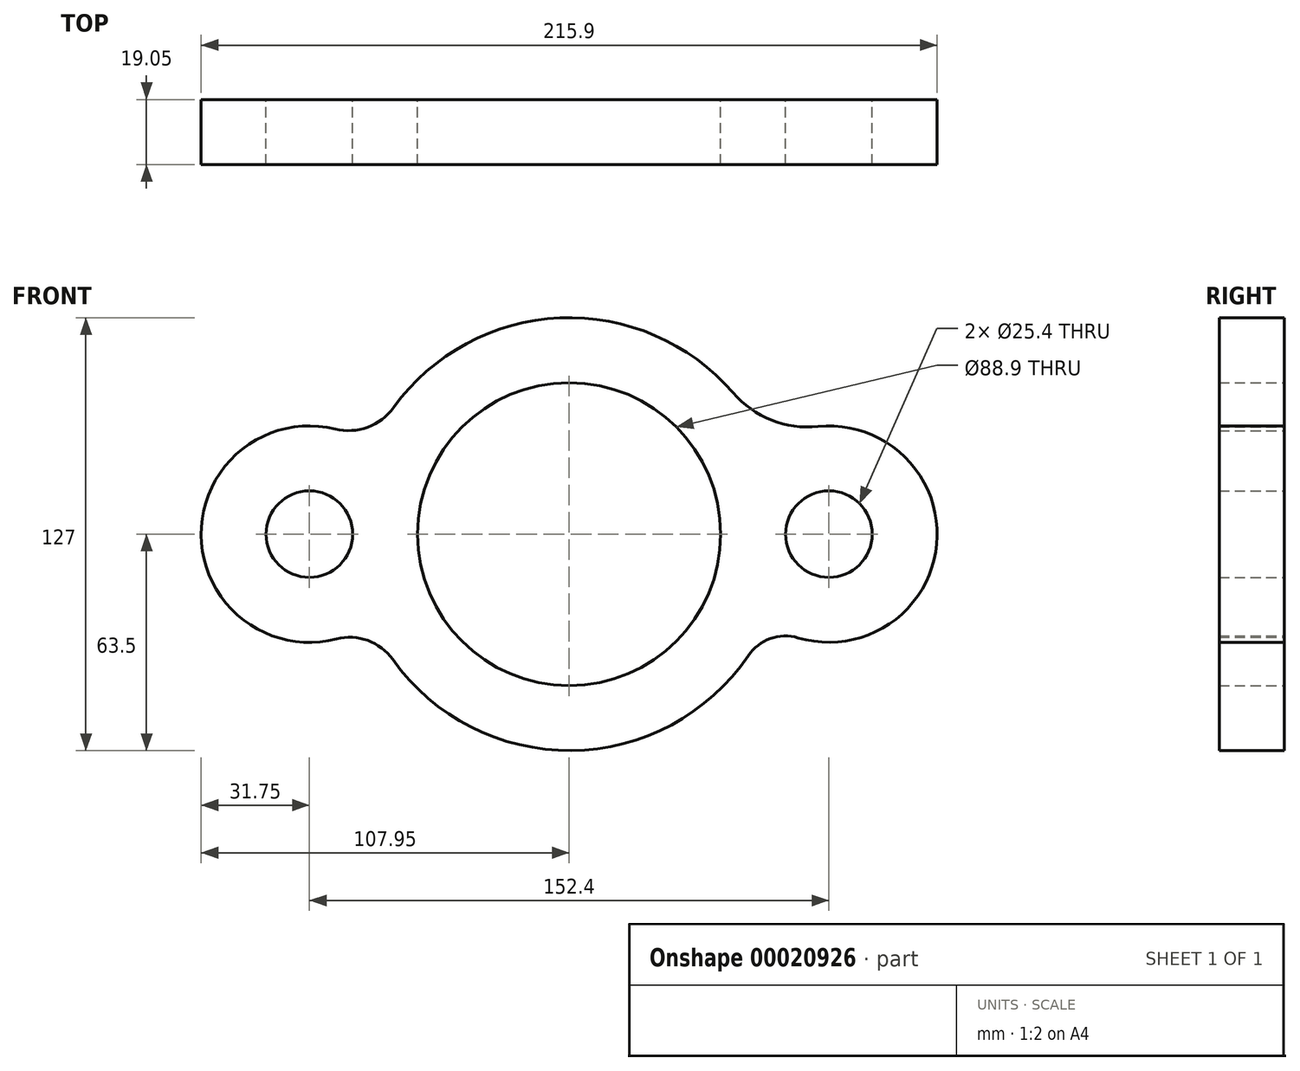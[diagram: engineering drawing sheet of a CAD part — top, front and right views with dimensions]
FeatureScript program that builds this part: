
annotation { "Feature Type Name" : "Feature", "Feature Type Description" : "" }
export const myFeature = defineFeature(function(context is Context, id is Id, definition is map)
    precondition{}
    {
        {
            var Q0;
            Q0=qCreatedBy(makeId("Front.planeOp"),FACE);
            var sketch = newSketch(context, id + "F0", { "sketchPlane" : qUnion([Q0])});
            skCircle(sketch, "E0", {"center": v(0, 0) * mm, "radius": 44.45 * mm});
            skCircle(sketch, "E1", {"center": v(-76.2, 0) * mm, "radius": 12.7 * mm});
            skCircle(sketch, "E2", {"center": v(76.2, 0) * mm, "radius": 12.7 * mm});
            skCircle(sketch, "E3", {"center": v(0, 0) * mm, "radius": 63.5 * mm});
            skCircle(sketch, "E4", {"center": v(76.2, 0) * mm, "radius": 31.75 * mm});
            skCircle(sketch, "E5", {"center": v(-76.2, 0) * mm, "radius": 31.75 * mm});
            skArc(sketch, "E6", {"start": v(48.07, 41.5) * mm, "mid": v(59.31, 33.5) * mm, "end": v(72.98, 31.59) * mm});
            skArc(sketch, "E7", {"start": v(-68.67, 30.84) * mm, "mid": v(-59.1, 31.39) * mm, "end": v(-51.48, 37.18) * mm});
            skArc(sketch, "E8", {"start": v(-51.78, -36.75) * mm, "mid": v(-59.08, -31.18) * mm, "end": v(-68.25, -30.74) * mm});
            skArc(sketch, "E9", {"start": v(67.18, -30.44) * mm, "mid": v(59, -30.67) * mm, "end": v(52.53, -35.67) * mm});
            skSolve(sketch);
        }
        {
            var Q0;
            {var subQ3=sQuery(id+"F0.wireOp",EDGE,"E0");var subQ5=sQuery(id+"F0.wireOp",EDGE,"E4");var subQ7=makeQuery(id+"F0.imprint","INTERSECT",VERTEX,{"derivedFrom":[subQ3,subQ5]});Q0=makeQuery(id+"F0.imprint","IMPRINT",FACE,{"disambiguationData":[TD([[makeQuery(id+"F0.imprint","IMPRINT",EDGE,{"disambiguationData":[TD([[subQ7,-1.0]])],"derivedFrom":subQ3}),-1.0]])]});}
            var Q1;
            {var subQ1=sQuery(id+"F0.wireOp",EDGE,"E3");var subQ5=makeQuery(id+"F0.imprint","INTERSECT",VERTEX,{"derivedFrom":[sQuery(id+"F0.wireOp",EDGE,"E1"),subQ1]});Q1=makeQuery(id+"F0.imprint","IMPRINT",FACE,{"disambiguationData":[TD([[makeQuery(id+"F0.imprint","IMPRINT",EDGE,{"disambiguationData":[TD([[subQ5,1.0]])],"derivedFrom":subQ1}),1.0]])]});}
            var Q2;
            {var subQ3=sQuery(id+"F0.wireOp",EDGE,"E0");var subQ5=sQuery(id+"F0.wireOp",EDGE,"E4");var subQ7=makeQuery(id+"F0.imprint","INTERSECT",VERTEX,{"derivedFrom":[subQ3,subQ5]});Q2=makeQuery(id+"F0.imprint","IMPRINT",FACE,{"disambiguationData":[TD([[makeQuery(id+"F0.imprint","IMPRINT",EDGE,{"disambiguationData":[TD([[subQ7,1.0]])],"derivedFrom":subQ3}),-1.0]])]});}
            var Q3;
            {var subQ1=sQuery(id+"F0.wireOp",EDGE,"E3");var subQ5=makeQuery(id+"F0.imprint","INTERSECT",VERTEX,{"derivedFrom":[sQuery(id+"F0.wireOp",EDGE,"E2"),subQ1]});Q3=makeQuery(id+"F0.imprint","IMPRINT",FACE,{"disambiguationData":[TD([[makeQuery(id+"F0.imprint","IMPRINT",EDGE,{"disambiguationData":[TD([[subQ5,-1.0]])],"derivedFrom":subQ1}),1.0]])]});}
            var Q4;
            {var subQ6=sQuery(id+"F0.wireOp",EDGE,"E2");Q4=makeQuery(id+"F0.imprint","IMPRINT",FACE,{"disambiguationData":[TD([[makeQuery(id+"F0.imprint","IMPRINT",EDGE,{"derivedFrom":subQ6}),-1.0]])]});}
            var Q5;
            {var subQ0=sQuery(id+"F0.wireOp",EDGE,"E6");Q5=makeQuery(id+"F0.imprint","IMPRINT",FACE,{"disambiguationData":[TD([[makeQuery(id+"F0.imprint","IMPRINT",EDGE,{"derivedFrom":subQ0}),-1.0]])]});}
            var Q6;
            {var subQ0=sQuery(id+"F0.wireOp",EDGE,"E9");Q6=makeQuery(id+"F0.imprint","IMPRINT",FACE,{"disambiguationData":[TD([[makeQuery(id+"F0.imprint","IMPRINT",EDGE,{"derivedFrom":subQ0}),-1.0]])]});}
            var Q7;
            {var subQ0=sQuery(id+"F0.wireOp",EDGE,"E7");Q7=makeQuery(id+"F0.imprint","IMPRINT",FACE,{"disambiguationData":[TD([[makeQuery(id+"F0.imprint","IMPRINT",EDGE,{"derivedFrom":subQ0}),-1.0]])]});}
            var Q8;
            {var subQ0=sQuery(id+"F0.wireOp",EDGE,"E8");Q8=makeQuery(id+"F0.imprint","IMPRINT",FACE,{"disambiguationData":[TD([[makeQuery(id+"F0.imprint","IMPRINT",EDGE,{"derivedFrom":subQ0}),-1.0]])]});}
            var Q9;
            {var subQ6=sQuery(id+"F0.wireOp",EDGE,"E1");Q9=makeQuery(id+"F0.imprint","IMPRINT",FACE,{"disambiguationData":[TD([[makeQuery(id+"F0.imprint","IMPRINT",EDGE,{"derivedFrom":subQ6}),-1.0]])]});}
            extrude(context, id + "F1", {"entities" : qUnion([Q0, Q1, Q2, Q3, Q4, Q5, Q6, Q7, Q8, Q9]), "depth" : 19.05 * mm});
        }
    });
